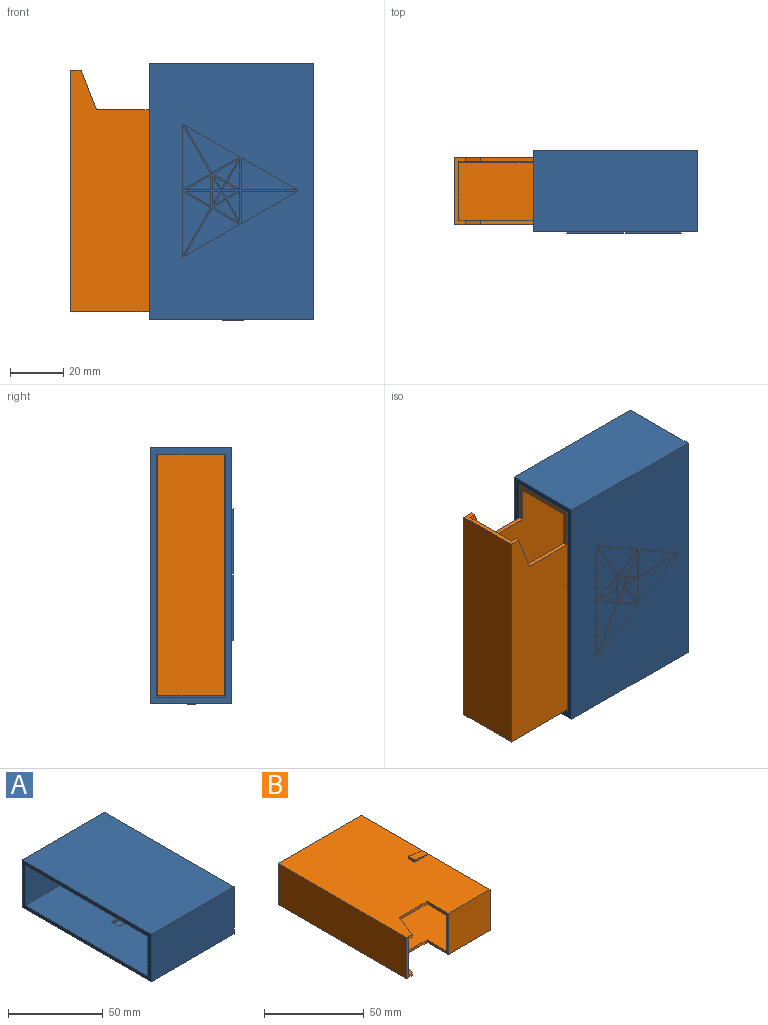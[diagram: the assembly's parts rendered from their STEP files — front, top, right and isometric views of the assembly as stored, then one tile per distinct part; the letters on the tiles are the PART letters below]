
ASSEMBLY  parts=2 mates=1
PART A: 167 faces, bbox 61.9x96.7x31.3 mm
  f0: plane 61.9x30.6mm, normal (0,1,0), area 1888.3mm2, adj f1,f2,f5,f7,f99,f100,f101,f102
  f1: plane 96.6x61.9mm, normal (0,0,-1), area 4996.7mm2, adj f0,f2,f5,f6,f27,f28,f29,f31
  f2: plane 96.6x30.6mm, normal (1,0,0), area 2577.4mm2, adj f0,f1,f6,f7,f19,f20,f21,f22
  f3: plane 91.8x59.5mm, normal (0,0,1), area 5249.3mm2, adj f5,f8,f9,f10,f15,f17,f18
  f4: plane 91.8x59.5mm, normal (0,0,-1), area 5249.3mm2, adj f5,f8,f9,f10,f11,f12,f13
  f5: plane 96.6x30.6mm, normal (-1,0,0), area 587.5mm2, adj f0,f1,f3,f4,f6,f7,f8,f9
  f6: plane 61.9x30.6mm, normal (0,-1,0), area 1894.1mm2, adj f1,f2,f5,f7
  f7: plane 96.6x61.9mm, normal (0,0,1), area 5979.5mm2, adj f0,f2,f5,f6
  f8: plane 59.5x25.8mm, normal (0,-1,0), area 1535.1mm2, adj f3,f4,f5,f10
  f9: plane 59.5x25.8mm, normal (0,1,0), area 1535.1mm2, adj f3,f4,f5,f10
  f10: plane 91.8x28.8mm, normal (-1,0,0), area 2006.7mm2, adj f3,f4,f8,f9,f11,f12,f14,f15
  f11: plane 38x1.5mm, normal (0,-1,0), area 57mm2, adj f4,f10,f13,f14
  f12: plane 38x1.5mm, normal (0,1,0), area 57mm2, adj f4,f10,f13,f14
  f13: plane 5.6x1.5mm, normal (1,0,0), area 8.4mm2, adj f4,f11,f12,f14
  f14: plane 38x5.6mm, normal (0,0,-1), area 212.8mm2, adj f10,f11,f12,f13
  f15: plane 38x1.5mm, normal (0,-1,0), area 57mm2, adj f3,f10,f16,f18
  f16: plane 38x5.6mm, normal (0,0,1), area 212.8mm2, adj f10,f15,f17,f18
  f17: plane 38x1.5mm, normal (0,1,0), area 57mm2, adj f3,f10,f16,f18
  f18: plane 5.6x1.5mm, normal (1,0,0), area 8.4mm2, adj f3,f15,f16,f17
  f19: plane 10x2.4mm, normal (0,0,1), area 24mm2, adj f2,f10,f24,f25
  f20: plane 10x2.4mm, normal (0,1,0), area 24mm2, adj f2,f10,f25,f26
  f21: plane 10x2.4mm, normal (0,0,-1), area 24mm2, adj f2,f10,f23,f26
  f22: plane 10x2.4mm, normal (0,-1,0), area 24mm2, adj f2,f10,f23,f24
  f23: cylinder r=5mm len=5mm, axis (-1,0,0), area 18.8mm2, adj f2,f10,f21,f22
  f24: cylinder r=5mm len=5mm, axis (1,0,0), area 18.8mm2, adj f2,f10,f19,f22
  f25: cylinder r=5mm len=5mm, axis (-1,0,0), area 18.8mm2, adj f2,f10,f19,f20
  f26: cylinder r=5mm len=5mm, axis (1,0,0), area 18.8mm2, adj f2,f10,f20,f21
  f27: plane 10.57x6.1mm, normal (0.5,0.87,0), area 8.1mm2, adj f1,f28,f29,f30
  f28: plane 18.3x10.57mm, normal (0.87,-0.5,0), area 14.1mm2, adj f1,f27,f29,f30
  f29: plane 24.4x0.67mm, normal (-1,0,0), area 16.3mm2, adj f1,f27,f28,f30
  f30: plane 24.4x10.57mm, normal (0,0,-1), area 128.9mm2, adj f27,f28,f29
  f31: plane 24.4x0.67mm, normal (-1,0,0), area 16.3mm2, adj f1,f32,f33,f34
  f32: plane 18.3x10.57mm, normal (0.87,0.5,0), area 14.1mm2, adj f1,f31,f33,f34
  f33: plane 10.57x6.1mm, normal (0.5,-0.87,0), area 8.1mm2, adj f1,f31,f32,f34
  f34: plane 24.4x10.57mm, normal (0,0,-1), area 128.9mm2, adj f31,f32,f33
  f35: plane 21.13x12.2mm, normal (0.5,-0.87,0), area 16.3mm2, adj f1,f36,f37,f38
  f36: plane 18.3x10.57mm, normal (-0.87,0.5,0), area 14.1mm2, adj f1,f35,f37,f38
  f37: plane 10.57x6.1mm, normal (0.5,0.87,0), area 8.1mm2, adj f1,f35,f36,f38
  f38: plane 21.13x18.3mm, normal (0,0,-1), area 128.9mm2, adj f35,f36,f37
  f39: plane 12.2x0.67mm, normal (-1,0,0), area 8.1mm2, adj f1,f40,f41,f42
  f40: plane 21.13x0.67mm, normal (0,1,0), area 14.1mm2, adj f1,f39,f41,f42
  f41: plane 21.13x12.2mm, normal (0.5,-0.87,0), area 16.3mm2, adj f1,f39,f40,f42
  f42: plane 21.13x12.2mm, normal (0,0,-1), area 128.9mm2, adj f39,f40,f41
  f43: plane 10.57x6.1mm, normal (0.5,-0.87,0), area 8.1mm2, adj f1,f44,f45,f46
  f44: plane 18.3x10.57mm, normal (-0.87,-0.5,0), area 14.1mm2, adj f1,f43,f45,f46
  f45: plane 21.13x12.2mm, normal (0.5,0.87,0), area 16.3mm2, adj f1,f43,f44,f46
  f46: plane 21.13x18.3mm, normal (0,0,-1), area 128.9mm2, adj f43,f44,f45
  f47: plane 12.2x0.67mm, normal (-1,0,0), area 8.1mm2, adj f1,f48,f49,f50
  f48: plane 21.13x12.2mm, normal (0.5,0.87,0), area 16.3mm2, adj f1,f47,f49,f50
  f49: plane 21.13x0.67mm, normal (0,-1,0), area 14.1mm2, adj f1,f47,f48,f50
  f50: plane 21.13x12.2mm, normal (0,0,-1), area 128.9mm2, adj f47,f48,f49
  f51: plane 5.62x0.67mm, normal (1,0,0), area 3.7mm2, adj f1,f52,f53,f54
  f52: plane 9.73x0.67mm, normal (0,-1,0), area 6.5mm2, adj f1,f51,f53,f54
  f53: plane 9.73x5.62mm, normal (-0.5,0.87,0), area 7.5mm2, adj f1,f51,f52,f54
  f54: plane 9.73x5.62mm, normal (0,0,-1), area 27.3mm2, adj f51,f52,f53
  f55: plane 4.43x2.56mm, normal (0.5,0.87,0), area 3.4mm2, adj f1,f56,f57,f58
  f56: plane 5.91x0.67mm, normal (0,-1,0), area 3.9mm2, adj f1,f55,f57,f58
  f57: plane 2.56x1.48mm, normal (-0.87,0.5,0), area 2mm2, adj f1,f55,f56,f58
  f58: plane 5.91x2.56mm, normal (0,0,-1), area 7.6mm2, adj f55,f56,f57
  f59: plane 5.12x2.95mm, normal (0.87,0.5,0), area 3.9mm2, adj f1,f60,f61,f62
  f60: plane 2.95x0.67mm, normal (0,-1,0), area 2mm2, adj f1,f59,f61,f62
  f61: plane 5.12x0.67mm, normal (-1,0,0), area 3.4mm2, adj f1,f59,f60,f62
  f62: plane 5.12x2.95mm, normal (0,0,-1), area 7.6mm2, adj f59,f60,f61
  f63: plane 5.62x0.67mm, normal (1,0,0), area 3.7mm2, adj f1,f64,f65,f66
  f64: plane 9.73x5.62mm, normal (-0.5,-0.87,0), area 7.5mm2, adj f1,f63,f65,f66
  f65: plane 9.73x0.67mm, normal (0,1,0), area 6.5mm2, adj f1,f63,f64,f66
  f66: plane 9.73x5.62mm, normal (0,0,-1), area 27.3mm2, adj f63,f64,f65
  f67: plane 5.91x0.67mm, normal (0,1,0), area 3.9mm2, adj f1,f68,f69,f70
  f68: plane 4.43x2.56mm, normal (0.5,-0.87,0), area 3.4mm2, adj f1,f67,f69,f70
  f69: plane 2.56x1.48mm, normal (-0.87,-0.5,0), area 2mm2, adj f1,f67,f68,f70
  f70: plane 5.91x2.56mm, normal (0,0,-1), area 7.6mm2, adj f67,f68,f69
  f71: plane 5.12x2.95mm, normal (0.87,-0.5,0), area 3.9mm2, adj f1,f72,f73,f74
  f72: plane 5.12x0.67mm, normal (-1,0,0), area 3.4mm2, adj f1,f71,f73,f74
  f73: plane 2.95x0.67mm, normal (0,1,0), area 2mm2, adj f1,f71,f72,f74
  f74: plane 5.12x2.95mm, normal (0,0,-1), area 7.6mm2, adj f71,f72,f73
  f75: plane 8.42x4.86mm, normal (0.87,0.5,0), area 6.5mm2, adj f1,f76,f77,f78
  f76: plane 9.73x5.62mm, normal (-0.5,-0.87,0), area 7.5mm2, adj f1,f75,f77,f78
  f77: plane 4.86x2.81mm, normal (-0.5,0.87,0), area 3.7mm2, adj f1,f75,f76,f78
  f78: plane 9.73x8.42mm, normal (0,0,-1), area 27.3mm2, adj f75,f76,f77
  f79: plane 4.43x2.56mm, normal (0.5,-0.87,0), area 3.4mm2, adj f1,f80,f81,f82
  f80: plane 5.12x2.95mm, normal (-0.87,0.5,0), area 3.9mm2, adj f1,f79,f81,f82
  f81: plane 2.56x1.48mm, normal (0.87,0.5,0), area 2mm2, adj f1,f79,f80,f82
  f82: plane 5.12x4.43mm, normal (0,0,-1), area 7.6mm2, adj f79,f80,f81
  f83: plane 8.42x4.86mm, normal (-0.87,-0.5,0), area 6.5mm2, adj f1,f84,f85,f86
  f84: plane 4.86x2.81mm, normal (-0.5,0.87,0), area 3.7mm2, adj f1,f83,f85,f86
  f85: plane 11.23x0.67mm, normal (1,0,0), area 7.5mm2, adj f1,f83,f84,f86
  f86: plane 11.23x4.86mm, normal (0,0,-1), area 27.3mm2, adj f83,f84,f85
  f87: plane 2.56x1.48mm, normal (0.87,-0.5,0), area 2mm2, adj f1,f88,f89,f90
  f88: plane 5.12x2.95mm, normal (-0.87,-0.5,0), area 3.9mm2, adj f1,f87,f89,f90
  f89: plane 4.43x2.56mm, normal (0.5,0.87,0), area 3.4mm2, adj f1,f87,f88,f90
  f90: plane 5.12x4.43mm, normal (0,0,-1), area 7.6mm2, adj f87,f88,f89
  f91: plane 8.42x4.86mm, normal (-0.87,0.5,0), area 6.5mm2, adj f1,f92,f93,f94
  f92: plane 11.23x0.67mm, normal (1,0,0), area 7.5mm2, adj f1,f91,f93,f94
  f93: plane 4.86x2.81mm, normal (-0.5,-0.87,0), area 3.7mm2, adj f1,f91,f92,f94
  f94: plane 11.23x4.86mm, normal (0,0,-1), area 27.3mm2, adj f91,f92,f93
  f95: plane 4.86x2.81mm, normal (-0.5,-0.87,0), area 3.7mm2, adj f1,f96,f97,f98
  f96: plane 9.73x5.62mm, normal (-0.5,0.87,0), area 7.5mm2, adj f1,f95,f97,f98
  f97: plane 8.42x4.86mm, normal (0.87,-0.5,0), area 6.5mm2, adj f1,f95,f96,f98
  f98: plane 9.73x8.42mm, normal (0,0,-1), area 27.3mm2, adj f95,f96,f97
  f99: extruded ~0.29x0.13mm, area 0mm2, adj f0,f100,f108,f109
  f100: extruded ~0.53x0.17mm, area 0.1mm2, adj f0,f99,f101,f109
  f101: extruded ~0.55x0.27mm, area 0.1mm2, adj f0,f100,f102,f109
  f102: plane 2.17x0.46mm, normal (-0.98,0,-0.21), area 0.3mm2, adj f0,f101,f103,f109
  f103: plane 0.47x0.13mm, normal (0,0,1), area 0.1mm2, adj f0,f102,f104,f109
  f104: plane 2.11x0.45mm, normal (0.98,0,0.21), area 0.3mm2, adj f0,f103,f105,f109
  f105: extruded ~0.29x0.14mm, area 0mm2, adj f0,f104,f106,f109
  f106: extruded ~0.25x0.13mm, area 0mm2, adj f0,f105,f107,f109
  f107: extruded ~0.25x0.13mm, area 0mm2, adj f0,f106,f108,f109
  f108: plane 0.39x0.13mm, normal (1,0,0), area 0.1mm2, adj f0,f99,f107,f109
  f109: plane 2.89x1.54mm, normal (0,1,0), area 1.5mm2, adj f99,f100,f101,f102,f103,f104,f105,f106
  f110: extruded ~0.22x0.13mm, area 0mm2, adj f0,f111,f117,f118
  f111: extruded ~0.16x0.13mm, area 0mm2, adj f0,f110,f112,f118
  f112: extruded ~0.17x0.13mm, area 0mm2, adj f0,f111,f113,f118
  f113: extruded ~0.22x0.13mm, area 0mm2, adj f0,f112,f114,f118
  f114: extruded ~0.22x0.13mm, area 0mm2, adj f0,f113,f115,f118
  f115: extruded ~0.16x0.13mm, area 0mm2, adj f0,f114,f116,f118
  f116: extruded ~0.17x0.13mm, area 0mm2, adj f0,f115,f117,f118
  f117: extruded ~0.23x0.13mm, area 0mm2, adj f0,f110,f116,f118
  f118: plane 0.54x0.52mm, normal (0,1,0), area 0.2mm2, adj f110,f111,f112,f113,f114,f115,f116,f117
  f119: plane 0.86x0.13mm, normal (0,0,1), area 0.1mm2, adj f0,f120,f140,f141
  f120: plane 0.39x0.13mm, normal (0.98,0,0.21), area 0.1mm2, adj f0,f119,f121,f141
  f121: plane 0.41x0.13mm, normal (0,0,-1), area 0.1mm2, adj f0,f120,f122,f141
  f122: plane 0.46x0.13mm, normal (0.98,0,0.22), area 0.1mm2, adj f0,f121,f123,f141
  f123: extruded ~0.26x0.13mm, area 0mm2, adj f0,f122,f124,f141
  f124: extruded ~0.34x0.13mm, area 0mm2, adj f0,f123,f125,f141
  f125: extruded ~0.39x0.13mm, area 0.1mm2, adj f0,f124,f126,f141
  f126: extruded ~0.5x0.13mm, area 0.1mm2, adj f0,f125,f127,f141
  f127: extruded ~0.36x0.29mm, area 0.1mm2, adj f0,f126,f128,f141
  f128: extruded ~0.42x0.13mm, area 0.1mm2, adj f0,f127,f129,f141
  f129: extruded ~0.25x0.13mm, area 0mm2, adj f0,f128,f130,f141
  f130: extruded ~0.23x0.13mm, area 0mm2, adj f0,f129,f131,f141
  f131: plane 0.38x0.18mm, normal (-0.91,0,-0.42), area 0.1mm2, adj f0,f130,f132,f141
  f132: extruded ~0.63x0.15mm, area 0.1mm2, adj f0,f131,f133,f141
  f133: extruded ~0.68x0.18mm, area 0.1mm2, adj f0,f132,f134,f141
  f134: extruded ~0.51x0.46mm, area 0.1mm2, adj f0,f133,f135,f141
  f135: extruded ~0.74x0.16mm, area 0.1mm2, adj f0,f134,f136,f141
  f136: extruded ~0.64x0.22mm, area 0.1mm2, adj f0,f135,f137,f141
  f137: extruded ~0.61x0.22mm, area 0.1mm2, adj f0,f136,f138,f141
  f138: extruded ~0.37x0.13mm, area 0mm2, adj f0,f137,f139,f141
  f139: extruded ~0.38x0.13mm, area 0.1mm2, adj f0,f138,f140,f141
  f140: plane 1.16x0.25mm, normal (-0.98,0,-0.21), area 0.2mm2, adj f0,f119,f139,f141
  f141: plane 2.3x1.93mm, normal (0,1,0), area 2.3mm2, adj f119,f120,f121,f122,f123,f124,f125,f126
  f142: extruded ~0.22x0.13mm, area 0mm2, adj f0,f143,f149,f150
  f143: extruded ~0.16x0.13mm, area 0mm2, adj f0,f142,f144,f150
  f144: extruded ~0.17x0.13mm, area 0mm2, adj f0,f143,f145,f150
  f145: extruded ~0.22x0.13mm, area 0mm2, adj f0,f144,f146,f150
  f146: extruded ~0.22x0.13mm, area 0mm2, adj f0,f145,f147,f150
  f147: extruded ~0.16x0.13mm, area 0mm2, adj f0,f146,f148,f150
  f148: extruded ~0.17x0.13mm, area 0mm2, adj f0,f147,f149,f150
  f149: extruded ~0.23x0.13mm, area 0mm2, adj f0,f142,f148,f150
  f150: plane 0.54x0.52mm, normal (0,1,0), area 0.2mm2, adj f142,f143,f144,f145,f146,f147,f148,f149
  f151: plane 2.23x0.47mm, normal (0.98,0,0.21), area 0.3mm2, adj f0,f152,f156,f157
  f152: plane 1.25x0.13mm, normal (0,0,-1), area 0.2mm2, adj f0,f151,f153,f157
  f153: plane 0.39x0.13mm, normal (-0.98,0,-0.21), area 0.1mm2, adj f0,f152,f154,f157
  f154: plane 0.78x0.13mm, normal (0,0,1), area 0.1mm2, adj f0,f153,f155,f157
  f155: plane 1.84x0.39mm, normal (-0.98,0,-0.21), area 0.2mm2, adj f0,f154,f156,f157
  f156: plane 0.47x0.13mm, normal (0,0,1), area 0.1mm2, adj f0,f151,f155,f157
  f157: plane 2.23x1.33mm, normal (0,1,0), area 1.3mm2, adj f151,f152,f153,f154,f155,f156
  f158: extruded ~0.22x0.13mm, area 0mm2, adj f0,f159,f165,f166
  f159: extruded ~0.16x0.13mm, area 0mm2, adj f0,f158,f160,f166
  f160: extruded ~0.17x0.13mm, area 0mm2, adj f0,f159,f161,f166
  f161: extruded ~0.22x0.13mm, area 0mm2, adj f0,f160,f162,f166
  f162: extruded ~0.22x0.13mm, area 0mm2, adj f0,f161,f163,f166
  f163: extruded ~0.16x0.13mm, area 0mm2, adj f0,f162,f164,f166
  f164: extruded ~0.17x0.13mm, area 0mm2, adj f0,f163,f165,f166
  f165: extruded ~0.23x0.13mm, area 0mm2, adj f0,f158,f164,f166
  f166: plane 0.54x0.52mm, normal (0,1,0), area 0.2mm2, adj f158,f159,f160,f161,f162,f163,f164,f165
PART B: 26 faces, bbox 59.2x91.2x28.2 mm
  f0: plane 91.2x59.2mm, normal (0,0,-1), area 5014.2mm2, adj f8,f10,f11,f12,f13,f14,f15,f16
  f1: plane 15x5.76mm, normal (0.93,-0.36,0), area 25.7mm2, adj f6,f9,f13,f17
  f2: plane 28x22mm, normal (0,1,0), area 616mm2, adj f3,f6,f7,f8
  f3: plane 88x22mm, normal (-1,0,0), area 1936mm2, adj f2,f4,f6,f7
  f4: plane 56x22mm, normal (0,-1,0), area 1232mm2, adj f3,f5,f6,f7
  f5: plane 89.6x22mm, normal (1,0,0), area 1971.2mm2, adj f4,f6,f7,f13
  f6: plane 89.6x56mm, normal (0,0,-1), area 4632mm2, adj f1,f2,f3,f4,f5,f8,f9,f13
  f7: plane 89.6x56mm, normal (0,0,1), area 4632mm2, adj f2,f3,f4,f5,f8,f10,f11,f13
  f8: plane 25.2x15mm, normal (-1,0,0), area 83.2mm2, adj f0,f2,f6,f7,f9,f11,f12,f17
  f9: plane 19.84x1.6mm, normal (0,-1,0), area 31.7mm2, adj f1,f6,f8,f17
  f10: plane 15x5.76mm, normal (0.93,-0.36,0), area 25.7mm2, adj f0,f7,f11,f13
  f11: plane 19.84x1.6mm, normal (0,-1,0), area 31.7mm2, adj f0,f7,f8,f10
  f12: plane 29.6x25.2mm, normal (0,-1,0), area 745.9mm2, adj f0,f8,f14,f17
  f13: plane 25.2x4mm, normal (0,-1,0), area 48mm2, adj f0,f1,f5,f6,f7,f10,f16,f17
  f14: plane 91.2x25.21mm, normal (1,0,0), area 2298.3mm2, adj f0,f12,f15,f17,f18,f19,f20,f22
  f15: plane 59.2x25.2mm, normal (0,1,0), area 1491.8mm2, adj f0,f14,f16,f17
  f16: plane 91.2x25.2mm, normal (-1,0,0), area 2298.2mm2, adj f0,f13,f15,f17
  f17: plane 91.2x59.2mm, normal (0,0,1), area 5014.2mm2, adj f1,f8,f9,f12,f13,f14,f15,f16
  f18: plane 10x1.5mm, normal (0,-1,0), area 7.5mm2, adj f0,f14,f19,f21
  f19: plane 10x4.4mm, normal (0.15,0,-0.99), area 44.5mm2, adj f14,f18,f20,f21
  f20: plane 10x1.5mm, normal (0,1,0), area 7.5mm2, adj f0,f14,f19,f21
  f21: plane 4.4x1.5mm, normal (-1,0,0), area 6.6mm2, adj f0,f18,f19,f20
  f22: plane 10x1.5mm, normal (0,1,0), area 7.5mm2, adj f14,f17,f23,f25
  f23: plane 10x4.4mm, normal (0.15,0,0.99), area 44.5mm2, adj f14,f22,f24,f25
  f24: plane 10x1.5mm, normal (0,-1,0), area 7.5mm2, adj f14,f17,f23,f25
  f25: plane 4.4x1.5mm, normal (-1,0,0), area 6.6mm2, adj f17,f22,f23,f24
PLACE A rot(axis=(-1,0,0),90deg) t=(-48.05,18.61,-0.4)mm
PLACE B rot(axis=(-1,0,0),90deg) t=(-77.75,-11.99,-0.1)mm
MATE slider A.f10 <-> B.f14  axis (-1,0,0) through (-18.15,0.61,45.5)mm
